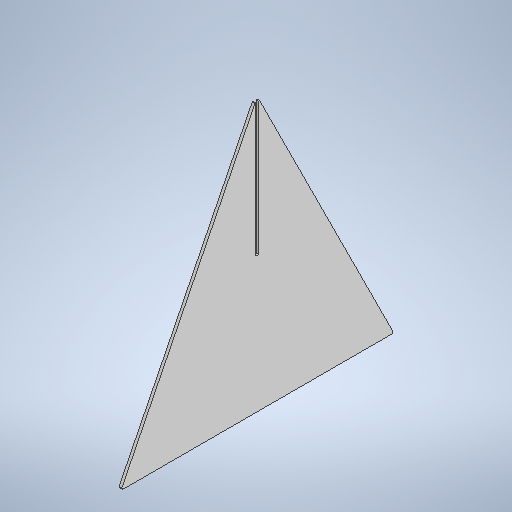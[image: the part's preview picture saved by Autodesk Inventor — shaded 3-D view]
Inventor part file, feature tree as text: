
AUTODESK INVENTOR PART (.ipt)
format: ipt  version: 2025 (Build 290162010, 162A)  size: 275,456 bytes
history: native  units: mm
features: other x3, sketch x2, sheet_metal_op x1, extrude x1
ambient origin geometry x8: Origin, YZ Plane, XZ Plane, XY Plane, X Axis, Y Axis, Z Axis, Center Point
bodies: Solid1 (feature_tree)
feature tree (7):
  sheet_metal_op  "Face1"
  extrude  "Extrusion1"  Depth=300.0mm
  other  "Corner Chamfer1"
  sketch  "Sketch1"  dims[d0=300.0mm d1=300.0mm]
  other  "Plate1"
  sketch  "Sketch2"  dims[d2=3.0mm d3=3.2mm d4=151.0mm d5=0.0mm d6=0.0mm d7=2.0mm d8=6.0mm d9=45.0deg]
  other  "Definition1"
